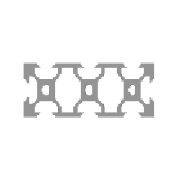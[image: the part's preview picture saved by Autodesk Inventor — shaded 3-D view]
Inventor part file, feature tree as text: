
AUTODESK INVENTOR PART (.ipt)
format: ipt  version: 2013 (Build 170138000, 138)  size: 242,688 bytes
history: native  units: mm
features: other x4, sketch x2, plane x1
ambient origin geometry x8: Origin, YZ Plane, XZ Plane, XY Plane, X Axis, Y Axis, Z Axis, Center Point
bodies: Solid1 (feature_tree), Body (feature_tree)
feature tree (7):
  other  "Driven Length"
  other  "Frame Generator"
  other  "Start Plane"
  other  "End Plane"
  sketch  "Sketch4"  dims[d0=10.0mm]
  plane  "Work Plane4"
  sketch  "Sketch5"  dims[d1=10.0mm d2=10.0mm d3=4.2mm d4=1.5mm d5=45.0deg d6=1.64mm d7=1.8mm d8=10.0mm d9=2.84mm d11=135.0deg d12=1.96mm d13=5.68mm d14=1.8mm d17=-0.0mm d18=475.0mm d19=0.13mm d20=0.0mm d23=90.0deg d22=475.0mm]
